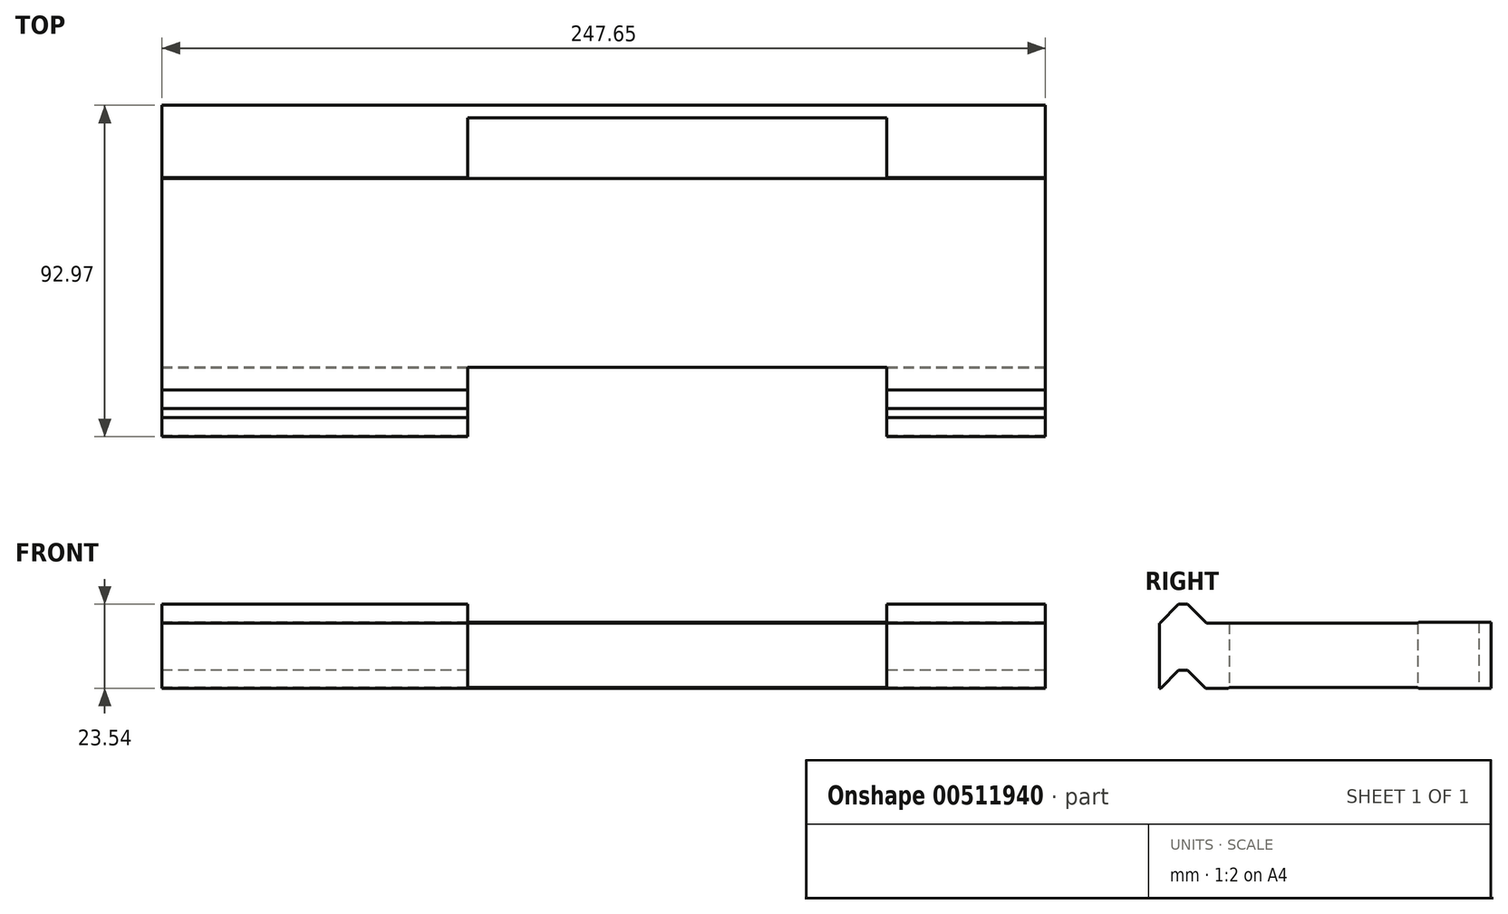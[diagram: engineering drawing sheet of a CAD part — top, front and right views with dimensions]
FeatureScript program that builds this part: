
annotation { "Feature Type Name" : "Feature", "Feature Type Description" : "" }
export const myFeature = defineFeature(function(context is Context, id is Id, definition is map)
    precondition{}
    {
        {
            var Q0;
            Q0=qCreatedBy(makeId("Right.planeOp"),FACE);
            var sketch = newSketch(context, id + "F0", { "sketchPlane" : qUnion([Q0])});
            skLineSegment(sketch, "E0", {"start": v(5.04, 5.04) * mm, "end": v(7.58, 5.04) * mm});
            skLineSegment(sketch, "E1", {"start": v(7.58, 5.04) * mm, "end": v(12.62, 0) * mm});
            skLineSegment(sketch, "E2", {"start": v(12.62, 0) * mm, "end": v(18.97, 0) * mm});
            skLineSegment(sketch, "E3", {"start": v(18.97, 0) * mm, "end": v(19.22, 0.25) * mm});
            skLineSegment(sketch, "E4", {"start": v(19.22, 0.25) * mm, "end": v(72.1, 0.25) * mm});
            skLineSegment(sketch, "E5", {"start": v(72.1, 0.25) * mm, "end": v(72.35, 0) * mm});
            skLineSegment(sketch, "E6", {"start": v(72.35, 0) * mm, "end": v(92.67, 0) * mm});
            skLineSegment(sketch, "E7", {"start": v(12.87, 18.24) * mm, "end": v(7.58, 23.54) * mm});
            skLineSegment(sketch, "E8", {"start": v(0, 0) * mm, "end": v(5.04, 5.04) * mm});
            skLineSegment(sketch, "E9", {"start": v(7.58, 23.54) * mm, "end": v(5.04, 23.54) * mm});
            skLineSegment(sketch, "E10", {"start": v(5.04, 23.54) * mm, "end": v(-0.25, 18.24) * mm});
            skCircle(sketch, "E11", {"center": v(6.3, -0.88) * mm, "radius": 5.08 * mm, "construction": true});
            skLineSegment(sketch, "E12", {"start": v(5.04, 5.04) * mm, "end": v(6.3, 6.3) * mm, "construction": true});
            skLineSegment(sketch, "E13", {"start": v(6.3, 6.3) * mm, "end": v(7.58, 5.04) * mm, "construction": true});
            skLineSegment(sketch, "E14", {"start": v(82.5, 0) * mm, "end": v(82.5, 18.5) * mm, "construction": true});
            skLineSegment(sketch, "E15", {"start": v(92.67, 0) * mm, "end": v(92.67, 18.5) * mm});
            skLineSegment(sketch, "E16", {"start": v(-0.25, 18.24) * mm, "end": v(-0.3, 18.24) * mm});
            skLineSegment(sketch, "E17", {"start": v(-0.3, 18.24) * mm, "end": v(-0.3, 0) * mm});
            skLineSegment(sketch, "E18", {"start": v(-0.3, 0) * mm, "end": v(0, 0) * mm});
            skLineSegment(sketch, "E19", {"start": v(6.3, 23.54) * mm, "end": v(6.3, 5.04) * mm, "construction": true});
            skLineSegment(sketch, "E20", {"start": v(92.67, 18.5) * mm, "end": v(72.35, 18.5) * mm});
            skLineSegment(sketch, "E21", {"start": v(72.35, 18.5) * mm, "end": v(72.1, 18.24) * mm});
            skLineSegment(sketch, "E22", {"start": v(72.1, 18.24) * mm, "end": v(12.87, 18.24) * mm});
            skLineSegment(sketch, "E23", {"start": v(5.04, 23.54) * mm, "end": v(6.3, 24.8) * mm, "construction": true});
            skLineSegment(sketch, "E24", {"start": v(6.3, 24.8) * mm, "end": v(7.58, 23.54) * mm, "construction": true});
            skLineSegment(sketch, "E25", {"start": v(0.24, 0.28) * mm, "end": v(6.3, 6.35) * mm, "construction": true});
            skLineSegment(sketch, "E26", {"start": v(6.3, 6.35) * mm, "end": v(12.1, 0.55) * mm, "construction": true});
            skSolve(sketch);
        }
        {
            var Q0;
            Q0=makeQuery(id+"F0.imprint","IMPRINT",FACE,{"disambiguationData":[TD([[makeQuery(id+"F0.imprint","IMPRINT",EDGE,{"derivedFrom":sQuery(id+"F0.wireOp",EDGE,"E0")}),1.0]])]});
            extrude(context, id + "F1", {"entities" : qUnion([Q0]), "depth" : 247.65 * mm, "offsetDistance" : 25.4 * mm});
        }
        {
            var Q0;
            Q0=makeQuery(id+"F1.opExtrude","SWEPT_FACE",FACE,{"disambiguationData":[OSD([sQuery(id+"F0.wireOp",EDGE,"E4")])]});
            var sketch = newSketch(context, id + "F2", { "sketchPlane" : qUnion([Q0])});
            skLineSegment(sketch, "E27.bottom", {"start": v(203.2, -89.15) * mm, "end": v(85.73, -89.15) * mm});
            skLineSegment(sketch, "E27.top", {"start": v(203.2, 4.78) * mm, "end": v(85.73, 4.78) * mm});
            skLineSegment(sketch, "E27.left", {"start": v(85.73, -71.42) * mm, "end": v(85.73, -89.15) * mm});
            skLineSegment(sketch, "E27.right", {"start": v(203.2, -71.42) * mm, "end": v(203.2, -89.15) * mm});
            skLineSegment(sketch, "E28", {"start": v(85.73, -71.42) * mm, "end": v(203.2, -71.42) * mm});
            skLineSegment(sketch, "E29", {"start": v(85.73, -33.32) * mm, "end": v(203.2, -33.32) * mm});
            skLineSegment(sketch, "E30.trimOffspring", {"start": v(85.73, 4.78) * mm, "end": v(85.73, -33.32) * mm});
            skLineSegment(sketch, "E31.trimOffspring", {"start": v(203.2, 4.78) * mm, "end": v(203.2, -33.32) * mm});
            skSolve(sketch);
        }
        {
            var Q0;
            Q0=makeQuery(id+"F2.imprint","IMPRINT",FACE,{"disambiguationData":[TD([[makeQuery(id+"F2.imprint","IMPRINT",EDGE,{"derivedFrom":sQuery(id+"F2.wireOp",EDGE,"E27.top")}),1.0]])]});
            var Q1;
            Q1=makeQuery(id+"F2.imprint","IMPRINT",FACE,{"disambiguationData":[TD([[makeQuery(id+"F2.imprint","IMPRINT",EDGE,{"derivedFrom":sQuery(id+"F2.wireOp",EDGE,"E27.bottom")}),-1.0]])]});
            extrude(context, id + "F3", {"entities" : qUnion([Q0, Q1]), "operationType" : NewBodyOperationType.REMOVE, "oppositeDirection" : true, "depth" : 25.4 * mm, "hasSecondDirection" : true, "secondDirectionOppositeDirection" : true, "secondDirectionDepth" : -25.4 * mm, "offsetDistance" : 25.4 * mm});
        }
    });
